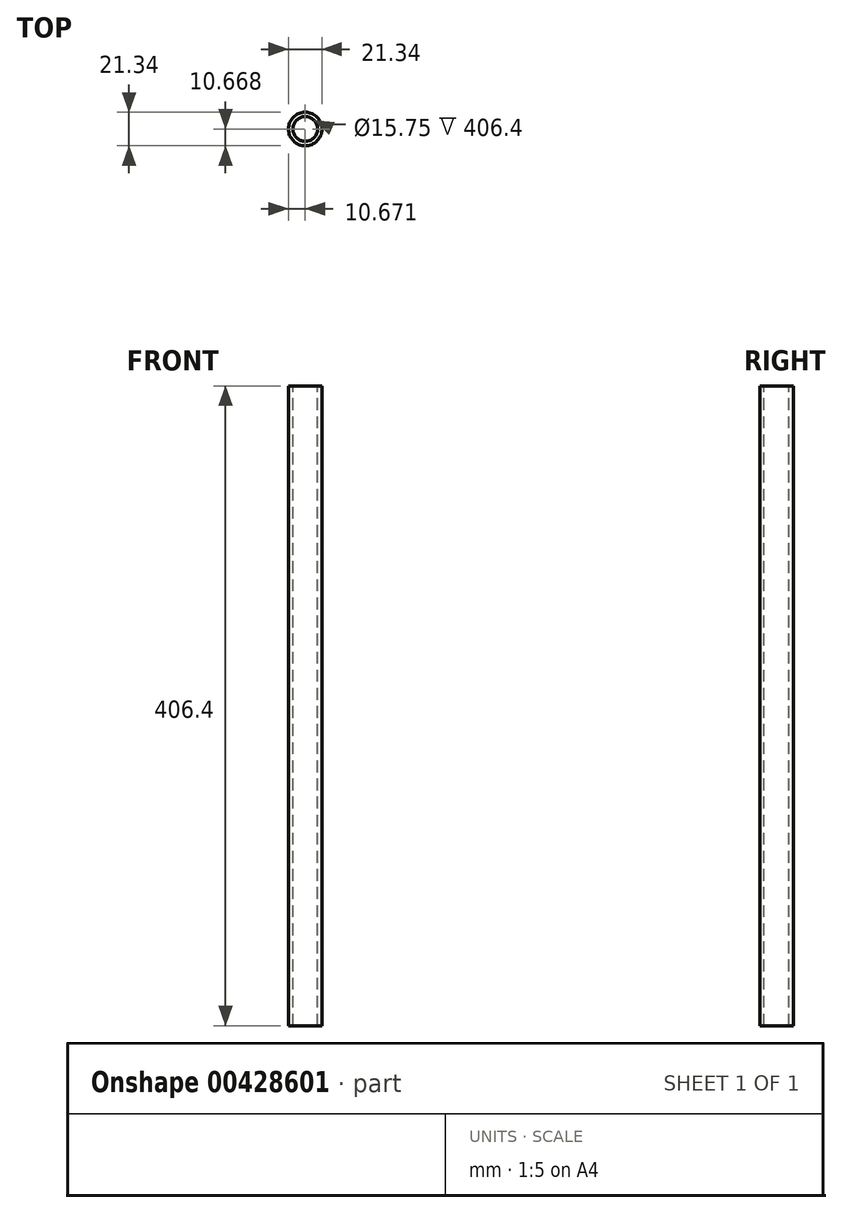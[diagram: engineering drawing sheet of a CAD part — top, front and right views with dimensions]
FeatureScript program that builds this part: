
annotation { "Feature Type Name" : "Feature", "Feature Type Description" : "" }
export const myFeature = defineFeature(function(context is Context, id is Id, definition is map)
    precondition{}
    {
        {
            var Q0;
            Q0=qCreatedBy(makeId("Top.planeOp"),FACE);
            var sketch = newSketch(context, id + "F0", { "sketchPlane" : qUnion([Q0])});
            skCircle(sketch, "E0", {"center": v(72.06, 47.03) * mm, "radius": 10.67 * mm});
            skSolve(sketch);
        }
        {
            var Q0;
            Q0=makeQuery(id+"F0.imprint","IMPRINT",FACE,{"disambiguationData":[TD([[makeQuery(id+"F0.imprint","IMPRINT",EDGE,{"derivedFrom":sQuery(id+"F0.wireOp",EDGE,"E0")}),1.0]])]});
            var sketch = newSketch(context, id + "F1", { "sketchPlane" : qUnion([Q0])});
            skCircle(sketch, "E1", {"center": v(72.06, 47.03) * mm, "radius": 7.87 * mm});
            skSolve(sketch);
        }
        {
            var Q0;
            Q0=makeQuery(id+"F1.imprint","IMPRINT",FACE,{"disambiguationData":[TD([[makeQuery(id+"F1.imprint","IMPRINT",EDGE,{"derivedFrom":sQuery(id+"F1.wireOp",EDGE,"E1")}),-1.0]])]});
            extrude(context, id + "F2", {"entities" : qUnion([Q0]), "oppositeDirection" : true, "depth" : 406.4 * mm});
        }
    });
